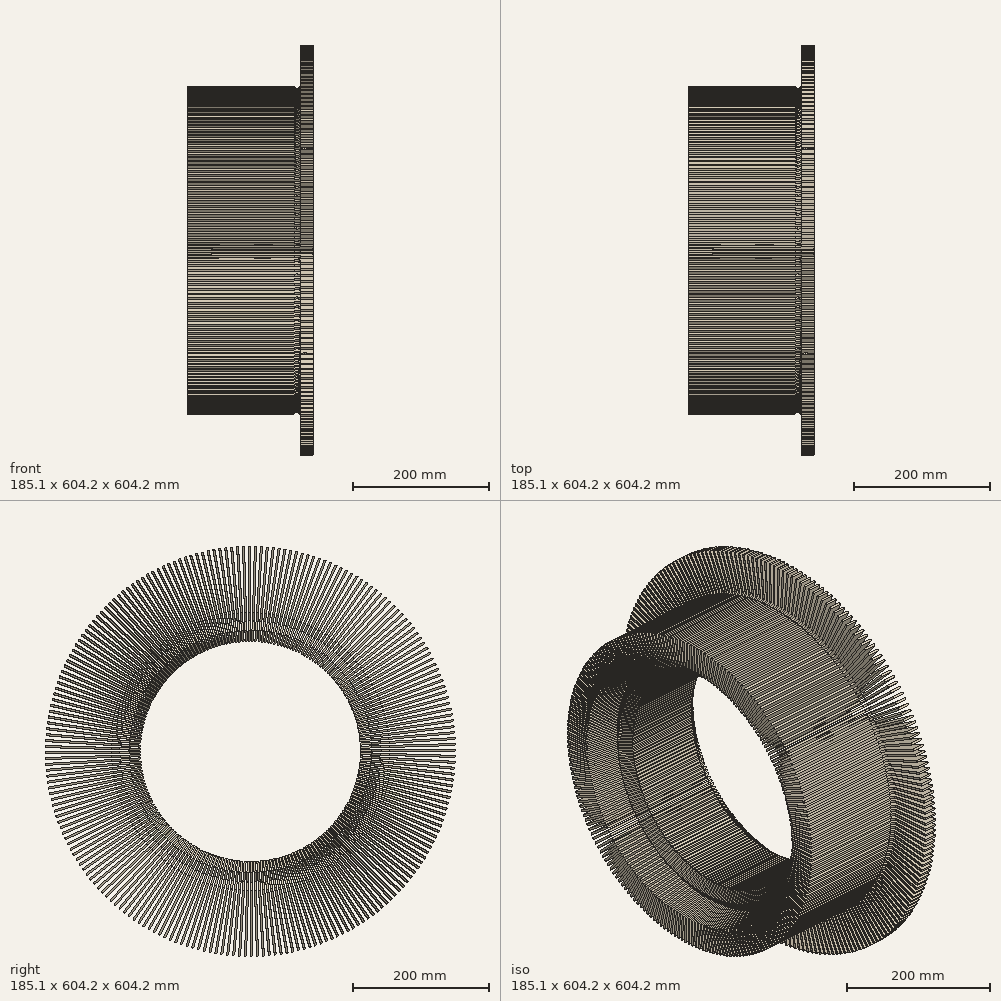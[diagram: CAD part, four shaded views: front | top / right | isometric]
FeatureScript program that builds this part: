
annotation { "Feature Type Name" : "Feature", "Feature Type Description" : "" }
export const myFeature = defineFeature(function(context is Context, id is Id, definition is map)
    precondition{}
    {
        {
            var Q0;
            Q0=qCreatedBy(makeId("Front.planeOp"),FACE);
            var sketch = newSketch(context, id + "F0", { "sketchPlane" : qUnion([Q0])});
            skLineSegment(sketch, "E0", {"start": v(79.42, 302.1) * mm, "end": v(60.42, 302.1) * mm});
            skLineSegment(sketch, "E1", {"start": v(60.42, 302.1) * mm, "end": v(60.42, 242.1) * mm});
            skPoint(sketch, "E2.second.point", {"position": v(51.33, 242.1) * mm});
            skPoint(sketch, "E2.third.point", {"position": v(46.48, 229.47) * mm});
            skLineSegment(sketch, "E3", {"start": v(51.33, 242.1) * mm, "end": v(-105.63, 242.1) * mm});
            skLineSegment(sketch, "E4", {"start": v(-105.63, 242.1) * mm, "end": v(-105.63, 202.86) * mm});
            skLineSegment(sketch, "E5", {"start": v(-105.63, 202.86) * mm, "end": v(-56.74, 192.37) * mm});
            skLineSegment(sketch, "E6", {"start": v(-70.04, 177.62) * mm, "end": v(-56.23, 162) * mm});
            skLineSegment(sketch, "E7", {"start": v(79.42, 302.1) * mm, "end": v(79.42, 204.59) * mm});
            skLineSegment(sketch, "E8", {"start": v(79.42, 204.59) * mm, "end": v(52.48, 192.37) * mm});
            skLineSegment(sketch, "E9", {"start": v(79.42, 302.1) * mm, "end": v(79.42, 161.1) * mm, "construction": true});
            skLineSegment(sketch, "E10", {"start": v(52.48, 192.37) * mm, "end": v(79.42, 178.6) * mm});
            skLineSegment(sketch, "E11", {"start": v(79.42, 178.6) * mm, "end": v(60.16, 162) * mm});
            skLineSegment(sketch, "E12", {"start": v(-56.74, 192.37) * mm, "end": v(64.95, 192.37) * mm, "construction": true});
            skCircle(sketch, "E13", {"center": v(5.68, 192.37) * mm, "radius": 13 * mm});
            skLineSegment(sketch, "E14", {"start": v(60.16, 162) * mm, "end": v(-56.23, 162) * mm});
            skPoint(sketch, "E15.orphan", {"position": v(86.94, 0) * mm});
            skLineSegment(sketch, "E16", {"start": v(-73.72, 0) * mm, "end": v(123.52, 0) * mm, "construction": true});
            skLineSegment(sketch, "E17", {"start": v(-70.04, 177.62) * mm, "end": v(-56.74, 192.37) * mm});
            skArc(sketch, "E18", {"start": v(51.33, 242.1) * mm, "mid": v(55.88, 238.85) * mm, "end": v(60.42, 242.1) * mm});
            skSolve(sketch);
        }
        {
            var Q0;
            Q0 = qSketchRegion(id + "F0", true);
            extrude(context, id + "F1", {"entities" : qUnion([Q0]), "depth" : 3 * mm});
        }
        {
            var Q0;
            Q0=makeQuery(id+"F1.opExtrude","SWEPT_BODY",BODY,{"disambiguationData":[OSD([sQuery(id+"F0.wireOp",EDGE,"E0"),sQuery(id+"F0.wireOp",EDGE,"E1"),sQuery(id+"F0.wireOp",EDGE,"E2"),sQuery(id+"F0.wireOp",EDGE,"E3"),sQuery(id+"F0.wireOp",EDGE,"E4"),sQuery(id+"F0.wireOp",EDGE,"E5"),sQuery(id+"F0.wireOp",EDGE,"fe14e24c-9013-4631-aaa9-38da1157594d"),sQuery(id+"F0.wireOp",EDGE,"E6"),sQuery(id+"F0.wireOp",EDGE,"E7"),sQuery(id+"F0.wireOp",EDGE,"E8"),sQuery(id+"F0.wireOp",EDGE,"E10"),sQuery(id+"F0.wireOp",EDGE,"E11"),sQuery(id+"F0.wireOp",EDGE,"E13"),sQuery(id+"F0.wireOp",EDGE,"E14")])]});
            var Q1;
            Q1=sQuery(id+"F0.wireOp",EDGE,"E16");
            circularPattern(context, id + "F2", {"entities" : qUnion([Q0]), "axis" : qUnion([Q1]), "angle" : 1.67 * degree, "instanceCount" : 216});
        }
    });
